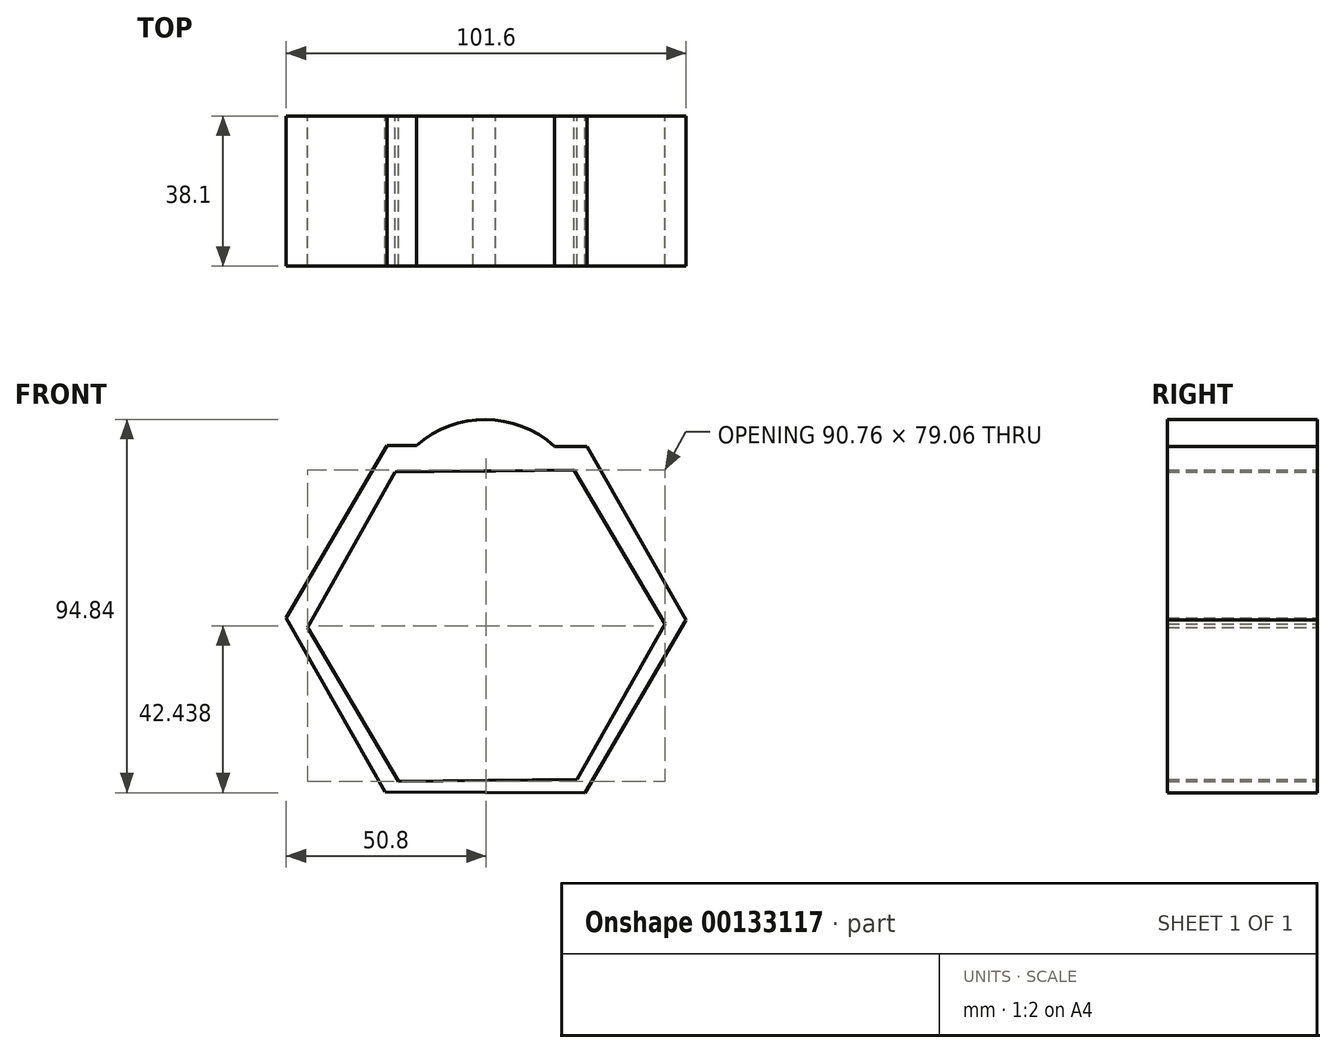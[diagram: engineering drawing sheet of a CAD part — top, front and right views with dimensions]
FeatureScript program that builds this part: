
annotation { "Feature Type Name" : "Feature", "Feature Type Description" : "" }
export const myFeature = defineFeature(function(context is Context, id is Id, definition is map)
    precondition{}
    {
        {
            var Q0;
            Q0=qCreatedBy(makeId("Front.planeOp"),FACE);
            var sketch = newSketch(context, id + "F0", { "sketchPlane" : qUnion([Q0])});
            skCircle(sketch, "E0.cCircle", {"center": v(0, -1.7) * mm, "radius": 39.3 * mm, "construction": true});
            skLineSegment(sketch, "E0.0", {"start": v(45.38, -1.23) * mm, "end": v(23.09, -40.76) * mm});
            skLineSegment(sketch, "E0.1", {"start": v(23.09, -40.76) * mm, "end": v(-22.3, -41.22) * mm});
            skLineSegment(sketch, "E0.2", {"start": v(-22.3, -41.22) * mm, "end": v(-45.38, -2.15) * mm});
            skLineSegment(sketch, "E0.3", {"start": v(-45.38, -2.15) * mm, "end": v(-23.09, 37.38) * mm});
            skLineSegment(sketch, "E0.4", {"start": v(-23.09, 37.38) * mm, "end": v(22.3, 37.84) * mm});
            skLineSegment(sketch, "E0.5", {"start": v(22.3, 37.84) * mm, "end": v(45.38, -1.23) * mm});
            skPoint(sketch, "E0.0.midPoint", {"position": v(34.24, -21) * mm});
            skCircle(sketch, "E1.cCircle", {"center": v(0, 0) * mm, "radius": 44 * mm, "construction": true});
            skLineSegment(sketch, "E1.0", {"start": v(25.63, 43.86) * mm, "end": v(50.8, -0.27) * mm});
            skLineSegment(sketch, "E1.1", {"start": v(50.8, -0.27) * mm, "end": v(25.17, -44.13) * mm});
            skLineSegment(sketch, "E1.2", {"start": v(25.17, -44.13) * mm, "end": v(-25.63, -43.86) * mm});
            skLineSegment(sketch, "E1.3", {"start": v(-25.63, -43.86) * mm, "end": v(-50.8, 0.27) * mm});
            skLineSegment(sketch, "E1.4", {"start": v(-50.8, 0.27) * mm, "end": v(-25.17, 44.13) * mm});
            skLineSegment(sketch, "E1.5", {"start": v(-25.17, 44.13) * mm, "end": v(25.63, 43.86) * mm});
            skPoint(sketch, "E1.0.midPoint", {"position": v(38.22, 21.8) * mm});
            skLineSegment(sketch, "E2.bottom", {"start": v(2.33, 37.64) * mm, "end": v(-3.3, 37.64) * mm});
            skLineSegment(sketch, "E2.top", {"start": v(2.33, -40.86) * mm, "end": v(-3.3, -40.86) * mm});
            skLineSegment(sketch, "E2.left", {"start": v(2.33, 37.64) * mm, "end": v(2.33, -40.86) * mm});
            skLineSegment(sketch, "E2.right", {"start": v(-3.3, 37.64) * mm, "end": v(-3.3, -40.86) * mm});
            skLineSegment(sketch, "E3.bottom", {"start": v(-4.93, 37.56) * mm, "end": v(2.33, 37.56) * mm});
            skLineSegment(sketch, "E3.top", {"start": v(-4.93, -40.86) * mm, "end": v(2.33, -40.86) * mm});
            skLineSegment(sketch, "E3.left", {"start": v(-4.93, 37.56) * mm, "end": v(-4.93, -40.86) * mm});
            skLineSegment(sketch, "E3.right", {"start": v(2.33, 37.56) * mm, "end": v(2.33, -40.86) * mm});
            skArc(sketch, "E4", {"start": v(22.3, 37.84) * mm, "mid": v(-0.53, 50.71) * mm, "end": v(-23.09, 37.38) * mm});
            skSolve(sketch);
        }
        {
            var Q0;
            Q0 = qSketchRegion(id + "F0", true);
            extrude(context, id + "F1", {"entities" : qUnion([Q0]), "depth" : 25.4 * mm});
        }
        {
            var Q0;
            Q0 = qSketchRegion(id + "F0", true);
            extrude(context, id + "F2", {"entities" : qUnion([Q0]), "operationType" : NewBodyOperationType.ADD, "endBound" : BoundingType.SYMMETRIC, "depth" : 25.4 * mm});
        }
    });
